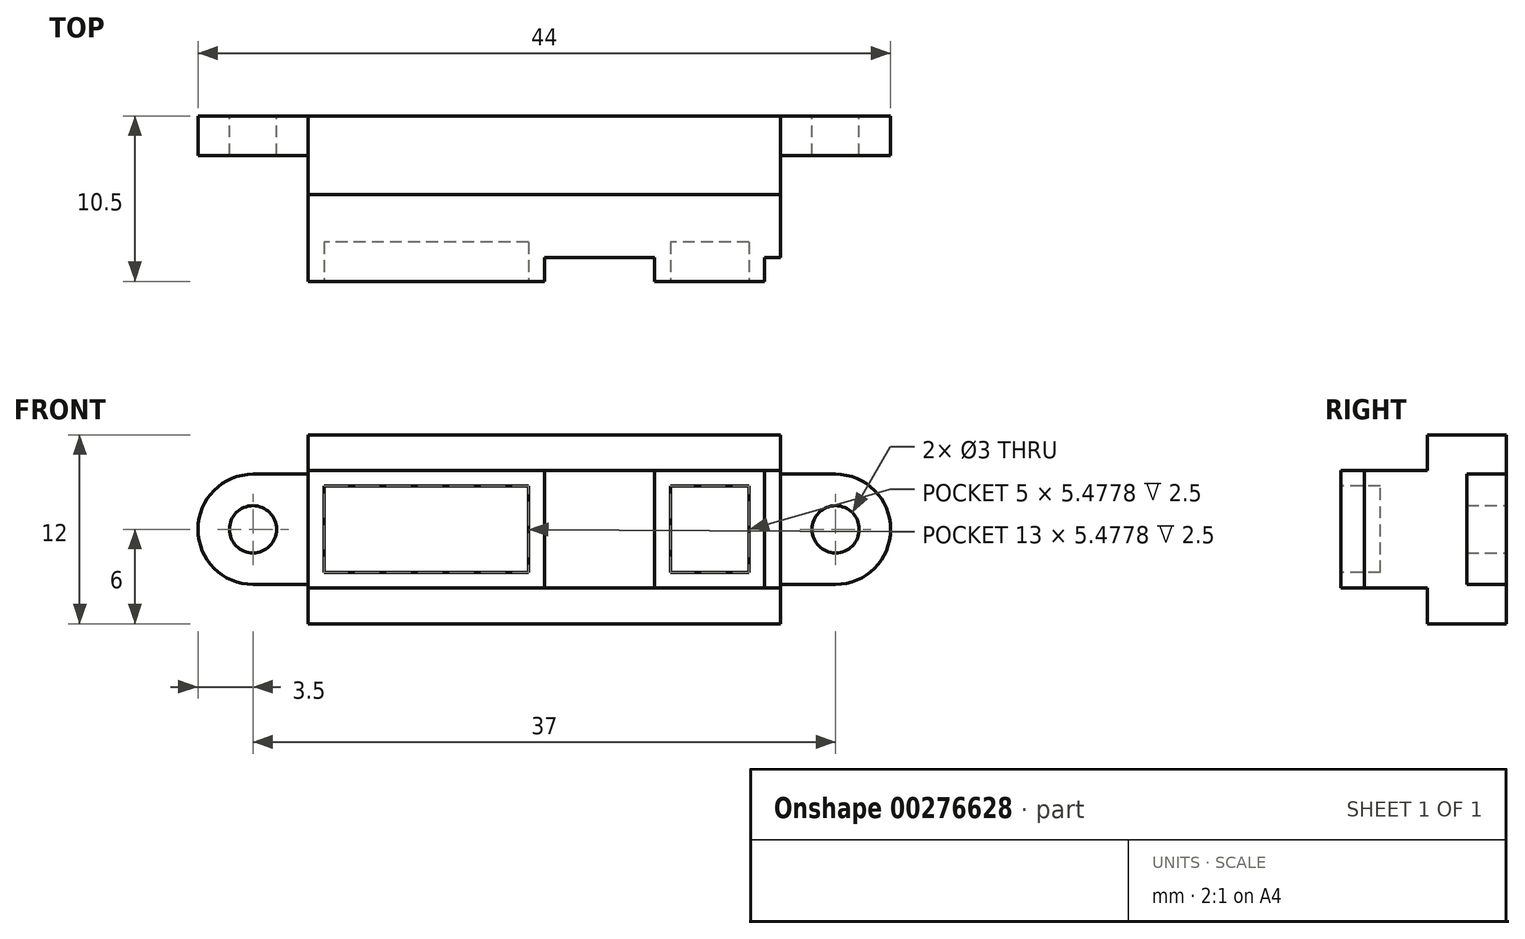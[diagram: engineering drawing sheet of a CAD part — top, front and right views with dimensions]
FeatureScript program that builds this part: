
annotation { "Feature Type Name" : "Feature", "Feature Type Description" : "" }
export const myFeature = defineFeature(function(context is Context, id is Id, definition is map)
    precondition{}
    {
        {
            var Q0;
            Q0=qCreatedBy(makeId("Front.planeOp"),FACE);
            var sketch = newSketch(context, id + "F0", { "sketchPlane" : qUnion([Q0])});
            skLineSegment(sketch, "E0.bottom", {"start": v(15, 6) * mm, "end": v(-15, 6) * mm});
            skLineSegment(sketch, "E0.top", {"start": v(15, -6) * mm, "end": v(-15, -6) * mm});
            skLineSegment(sketch, "E0.left", {"start": v(15, 6) * mm, "end": v(15, -6) * mm});
            skLineSegment(sketch, "E0.right", {"start": v(-15, 6) * mm, "end": v(-15, -6) * mm});
            skPoint(sketch, "E0.middle", {"position": v(0, 0) * mm});
            skSolve(sketch);
        }
        {
            var Q0;
            Q0 = qSketchRegion(id + "F0", true);
            extrude(context, id + "F1", {"entities" : qUnion([Q0]), "depth" : 5 * mm});
        }
        {
            var Q0;
            Q0=makeQuery(id+"F1.opExtrude","CAP_FACE",FACE,{"disambiguationData":[OSD([sQuery(id+"F0.wireOp",EDGE,"E0.bottom"),sQuery(id+"F0.wireOp",EDGE,"E0.top"),sQuery(id+"F0.wireOp",EDGE,"E0.left"),sQuery(id+"F0.wireOp",EDGE,"E0.right")])],"isStart":false});
            var sketch = newSketch(context, id + "F2", { "sketchPlane" : qUnion([Q0])});
            skLineSegment(sketch, "E1.bottom", {"start": v(15, 3.74) * mm, "end": v(-15, 3.74) * mm});
            skLineSegment(sketch, "E1.top", {"start": v(15, -3.74) * mm, "end": v(-15, -3.74) * mm});
            skLineSegment(sketch, "E1.left", {"start": v(15, 3.74) * mm, "end": v(15, -3.74) * mm});
            skLineSegment(sketch, "E1.right", {"start": v(-15, 3.74) * mm, "end": v(-15, -3.74) * mm});
            skPoint(sketch, "E1.middle", {"position": v(0, 0) * mm});
            skSolve(sketch);
        }
        {
            var Q0;
            Q0 = qSketchRegion(id + "F2", true);
            extrude(context, id + "F3", {"entities" : qUnion([Q0]), "operationType" : NewBodyOperationType.ADD, "depth" : 4 * mm});
        }
        {
            var Q0;
            Q0=makeQuery(id+"F3.opExtrude","CAP_FACE",FACE,{"disambiguationData":[OSD([sQuery(id+"F2.wireOp",EDGE,"E1.bottom"),sQuery(id+"F2.wireOp",EDGE,"E1.top"),sQuery(id+"F2.wireOp",EDGE,"E1.left"),sQuery(id+"F2.wireOp",EDGE,"E1.right")])],"isStart":false});
            var sketch = newSketch(context, id + "F4", { "sketchPlane" : qUnion([Q0])});
            skLineSegment(sketch, "E2.bottom", {"start": v(-15, 3.74) * mm, "end": v(0, 3.74) * mm});
            skLineSegment(sketch, "E2.top", {"start": v(-15, -3.74) * mm, "end": v(0, -3.74) * mm});
            skLineSegment(sketch, "E2.left", {"start": v(-15, 3.74) * mm, "end": v(-15, -3.74) * mm});
            skLineSegment(sketch, "E2.right", {"start": v(0, 3.74) * mm, "end": v(0, -3.74) * mm});
            skPoint(sketch, "E2.middle", {"position": v(-7.5, 0) * mm});
            skLineSegment(sketch, "E3.bottom", {"start": v(14, 3.74) * mm, "end": v(7, 3.74) * mm});
            skLineSegment(sketch, "E3.top", {"start": v(14, -3.74) * mm, "end": v(7, -3.74) * mm});
            skLineSegment(sketch, "E3.left", {"start": v(14, 3.74) * mm, "end": v(14, -3.74) * mm});
            skLineSegment(sketch, "E3.right", {"start": v(7, 3.74) * mm, "end": v(7, -3.74) * mm});
            skPoint(sketch, "E3.middle", {"position": v(10.5, 0) * mm});
            skSolve(sketch);
        }
        {
            var Q0;
            Q0 = qSketchRegion(id + "F4", true);
            extrude(context, id + "F5", {"entities" : qUnion([Q0]), "operationType" : NewBodyOperationType.ADD, "depth" : 1.5 * mm});
        }
        {
            var Q0;
            Q0=makeQuery(id+"F5.opExtrude","CAP_FACE",FACE,{"disambiguationData":[OSD([sQuery(id+"F4.wireOp",EDGE,"E2.bottom"),sQuery(id+"F4.wireOp",EDGE,"E2.top"),sQuery(id+"F4.wireOp",EDGE,"E2.left"),sQuery(id+"F4.wireOp",EDGE,"E2.right")])],"isStart":false});
            var sketch = newSketch(context, id + "F6", { "sketchPlane" : qUnion([Q0])});
            skLineSegment(sketch, "E4.bottom", {"start": v(-1, 2.74) * mm, "end": v(-14, 2.74) * mm});
            skLineSegment(sketch, "E4.top", {"start": v(-1, -2.74) * mm, "end": v(-14, -2.74) * mm});
            skLineSegment(sketch, "E4.left", {"start": v(-1, 2.74) * mm, "end": v(-1, -2.74) * mm});
            skLineSegment(sketch, "E4.right", {"start": v(-14, 2.74) * mm, "end": v(-14, -2.74) * mm});
            skPoint(sketch, "E4.middle", {"position": v(-7.5, 0) * mm});
            skPoint(sketch, "E4.middle.positionSnap0", {"position": v(-7.5, 3.74) * mm});
            skPoint(sketch, "E4.centerSnap0", {"position": v(-7.5, 3.74) * mm});
            skLineSegment(sketch, "E5.0", {"start": v(14, -3.74) * mm, "end": v(7, -3.74) * mm});
            skLineSegment(sketch, "E6.0", {"start": v(7, 3.74) * mm, "end": v(7, -3.74) * mm});
            skLineSegment(sketch, "E6.1", {"start": v(14, 3.74) * mm, "end": v(7, 3.74) * mm});
            skLineSegment(sketch, "E6.2", {"start": v(14, 3.74) * mm, "end": v(14, -3.74) * mm});
            skLineSegment(sketch, "E6.3.0", {"start": v(14, 3.74) * mm, "end": v(7, 3.74) * mm});
            skLineSegment(sketch, "E6.3.1", {"start": v(7, 3.74) * mm, "end": v(7, -3.74) * mm});
            skLineSegment(sketch, "E6.3.2", {"start": v(7, -3.74) * mm, "end": v(14, -3.74) * mm});
            skLineSegment(sketch, "E6.3.3", {"start": v(14, -3.74) * mm, "end": v(14, 3.74) * mm});
            skLineSegment(sketch, "E7.0", {"start": v(13, 2.74) * mm, "end": v(8, 2.74) * mm});
            skLineSegment(sketch, "E7.1", {"start": v(13, -2.74) * mm, "end": v(13, 2.74) * mm});
            skLineSegment(sketch, "E7.2", {"start": v(8, -2.74) * mm, "end": v(13, -2.74) * mm});
            skLineSegment(sketch, "E7.3", {"start": v(8, 2.74) * mm, "end": v(8, -2.74) * mm});
            skSolve(sketch);
        }
        {
            var Q0;
            Q0=makeQuery(id+"F6.imprint","IMPRINT",FACE,{"disambiguationData":[TD([[makeQuery(id+"F6.imprint","IMPRINT",EDGE,{"derivedFrom":sQuery(id+"F6.wireOp",EDGE,"E4.bottom")}),1.0]])]});
            var Q1;
            Q1=makeQuery(id+"F6.imprint","IMPRINT",FACE,{"disambiguationData":[TD([[makeQuery(id+"F6.imprint","IMPRINT",EDGE,{"derivedFrom":sQuery(id+"F6.wireOp",EDGE,"E7.0")}),1.0]])]});
            extrude(context, id + "F7", {"entities" : qUnion([Q0, Q1]), "operationType" : NewBodyOperationType.REMOVE, "oppositeDirection" : true, "depth" : 2.5 * mm});
        }
        {
            var Q0;
            Q0=makeQuery(id+"F1.opExtrude","CAP_FACE",FACE,{"disambiguationData":[OSD([sQuery(id+"F0.wireOp",EDGE,"E0.bottom"),sQuery(id+"F0.wireOp",EDGE,"E0.top"),sQuery(id+"F0.wireOp",EDGE,"E0.left"),sQuery(id+"F0.wireOp",EDGE,"E0.right")])],"isStart":true});
            var sketch = newSketch(context, id + "F8", { "sketchPlane" : qUnion([Q0])});
            skCircle(sketch, "E8", {"center": v(-18.5, 0) * mm, "radius": 1.5 * mm});
            skPoint(sketch, "E8.centerSnap0", {"position": v(-15, 0) * mm});
            skLineSegment(sketch, "E9", {"start": v(-15, 0) * mm, "end": v(-22, 0) * mm, "construction": true});
            skArc(sketch, "E10", {"start": v(-18.5, 3.5) * mm, "mid": v(-22, 0) * mm, "end": v(-18.5, -3.5) * mm});
            skLineSegment(sketch, "E11", {"start": v(-18.5, 0) * mm, "end": v(-18.5, 3.5) * mm, "construction": true});
            skLineSegment(sketch, "E12", {"start": v(-18.5, 3.5) * mm, "end": v(-15, 3.5) * mm});
            skLineSegment(sketch, "E13", {"start": v(-18.5, 0) * mm, "end": v(-18.5, -3.5) * mm, "construction": true});
            skLineSegment(sketch, "E14", {"start": v(-18.5, -3.5) * mm, "end": v(-15, -3.5) * mm});
            skLineSegment(sketch, "E15", {"start": v(0, 6) * mm, "end": v(0, -6) * mm, "construction": true});
            skLineSegment(sketch, "E16.MirrorCS", {"start": v(18.5, 3.5) * mm, "end": v(15, 3.5) * mm});
            skArc(sketch, "E17.MirrorCS", {"start": v(18.5, 3.5) * mm, "mid": v(22, 0) * mm, "end": v(18.5, -3.5) * mm});
            skCircle(sketch, "E18.MirrorC", {"center": v(18.5, 0) * mm, "radius": 1.5 * mm});
            skLineSegment(sketch, "E19.MirrorCS", {"start": v(18.5, -3.5) * mm, "end": v(15, -3.5) * mm});
            skSolve(sketch);
        }
        {
            var Q0;
            Q0=makeQuery(id+"F8.imprint","IMPRINT",FACE,{"disambiguationData":[TD([[makeQuery(id+"F8.imprint","IMPRINT",EDGE,{"derivedFrom":sQuery(id+"F8.wireOp",EDGE,"E8")}),-1.0]])]});
            var Q1;
            {var subQ1=sQuery(id+"F8.wireOp",EDGE,"E16.MirrorCS");Q1=makeQuery(id+"F8.imprint","IMPRINT",FACE,{"disambiguationData":[TD([[makeQuery(id+"F8.imprint","IMPRINT",EDGE,{"derivedFrom":subQ1}),1.0]])]});}
            extrude(context, id + "F9", {"entities" : qUnion([Q0, Q1]), "operationType" : NewBodyOperationType.ADD, "oppositeDirection" : true, "depth" : 2.5 * mm});
        }
    });
